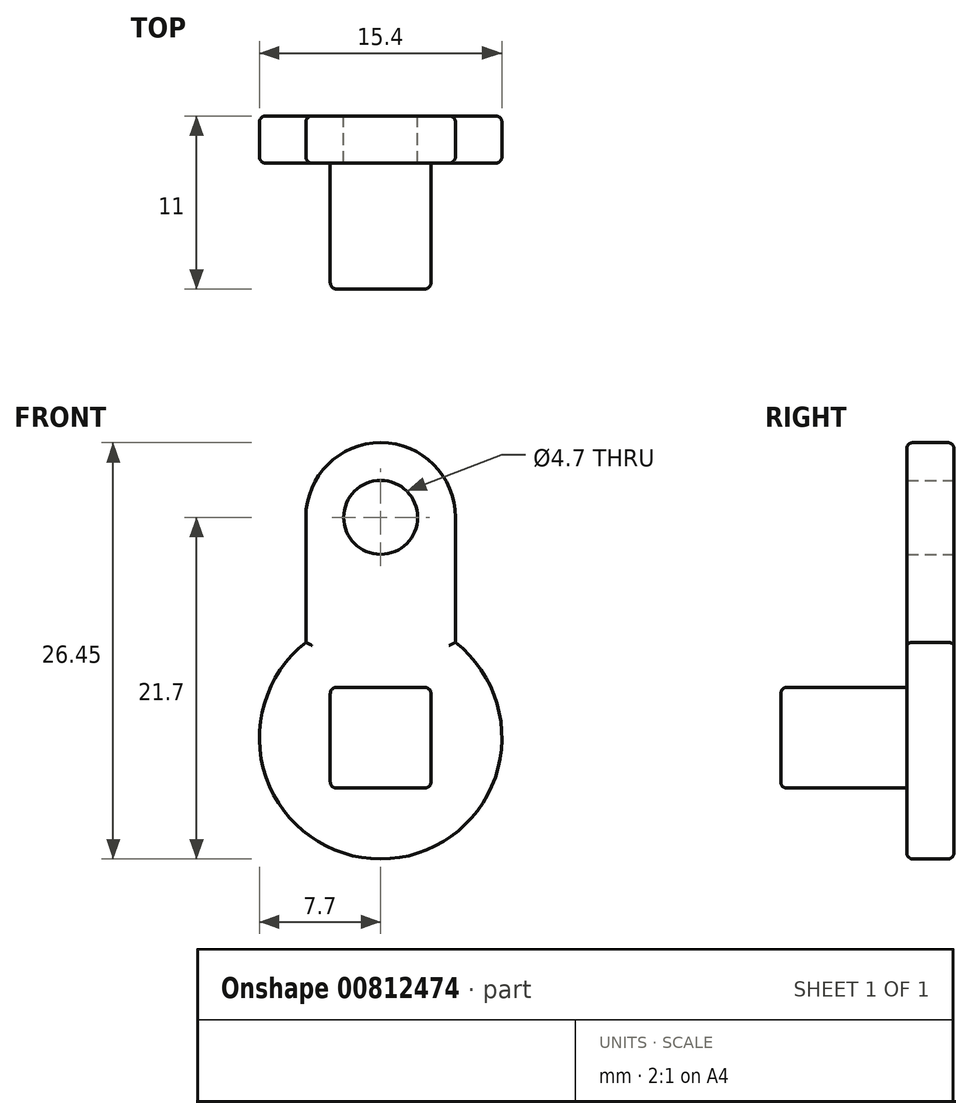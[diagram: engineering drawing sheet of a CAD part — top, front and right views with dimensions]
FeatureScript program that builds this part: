
annotation { "Feature Type Name" : "Feature", "Feature Type Description" : "" }
export const myFeature = defineFeature(function(context is Context, id is Id, definition is map)
    precondition{}
    {
        {
            var Q0;
            Q0=qCreatedBy(makeId("Front.planeOp"),FACE);
            var sketch = newSketch(context, id + "F0", { "sketchPlane" : qUnion([Q0])});
            skCircle(sketch, "E0", {"center": v(0, 0) * mm, "radius": 7.7 * mm});
            skCircle(sketch, "E1", {"center": v(0, 14) * mm, "radius": 4.75 * mm});
            skLineSegment(sketch, "E2", {"start": v(-4.75, 14.01) * mm, "end": v(-4.75, 6.06) * mm});
            skLineSegment(sketch, "E3", {"start": v(4.75, 14) * mm, "end": v(4.75, 6.06) * mm});
            skCircle(sketch, "E4", {"center": v(0, 14) * mm, "radius": 2.35 * mm});
            skSolve(sketch);
        }
        {
            var Q0;
            Q0 = qSketchRegion(id + "F0", true);
            extrude(context, id + "F1", {"entities" : qUnion([Q0]), "depth" : 3 * mm, "offsetDistance" : 25 * mm});
        }
        {
            var Q0;
            Q0=makeQuery(id+"F1.opExtrude","CAP_FACE",FACE,{"disambiguationData":[OSD([sQuery(id+"F0.wireOp",EDGE,"E0"),sQuery(id+"F0.wireOp",EDGE,"E1"),sQuery(id+"F0.wireOp",EDGE,"E2"),sQuery(id+"F0.wireOp",EDGE,"E3"),sQuery(id+"F0.wireOp",EDGE,"E4")])],"isStart":false});
            var sketch = newSketch(context, id + "F2", { "sketchPlane" : qUnion([Q0])});
            skLineSegment(sketch, "E5.bottom", {"start": v(-3.2, 3.2) * mm, "end": v(3.2, 3.2) * mm});
            skLineSegment(sketch, "E5.top", {"start": v(-3.2, -3.2) * mm, "end": v(3.2, -3.2) * mm});
            skLineSegment(sketch, "E5.left", {"start": v(-3.2, 3.2) * mm, "end": v(-3.2, -3.2) * mm});
            skLineSegment(sketch, "E5.right", {"start": v(3.2, 3.2) * mm, "end": v(3.2, -3.2) * mm});
            skSolve(sketch);
        }
        {
            var Q0;
            Q0=makeQuery(id+"F2.imprint","IMPRINT",FACE,{"disambiguationData":[TD([[makeQuery(id+"F2.imprint","IMPRINT",EDGE,{"derivedFrom":sQuery(id+"F2.wireOp",EDGE,"E5.bottom")}),-1.0]])]});
            extrude(context, id + "F3", {"entities" : qUnion([Q0]), "operationType" : NewBodyOperationType.ADD, "depth" : 8 * mm, "offsetDistance" : 25 * mm});
        }
        {
            var Q0;
            Q0=makeQuery(id+"F3.opExtrude","CAP_EDGE",EDGE,{"disambiguationData":[OSD([sQuery(id+"F2.wireOp",EDGE,"E5.left")])],"isStart":false});
            var Q1;
            Q1=makeQuery(id+"F3.opExtrude","SWEPT_EDGE",EDGE,{"disambiguationData":[OSD([sQuery(id+"F2.wireOp",EDGE,"E5.bottom"),sQuery(id+"F2.wireOp",EDGE,"E5.left")])]});
            var Q2;
            Q2=makeQuery(id+"F3.opExtrude","CAP_EDGE",EDGE,{"disambiguationData":[OSD([sQuery(id+"F2.wireOp",EDGE,"E5.bottom")])],"isStart":false});
            var Q3;
            Q3=makeQuery(id+"F3.opExtrude","CAP_EDGE",EDGE,{"disambiguationData":[OSD([sQuery(id+"F2.wireOp",EDGE,"E5.top")])],"isStart":false});
            var Q4;
            Q4=makeQuery(id+"F3.opExtrude","CAP_EDGE",EDGE,{"disambiguationData":[OSD([sQuery(id+"F2.wireOp",EDGE,"E5.right")])],"isStart":false});
            var Q5;
            Q5=makeQuery(id+"F3.opExtrude","SWEPT_EDGE",EDGE,{"disambiguationData":[OSD([sQuery(id+"F2.wireOp",EDGE,"E5.top"),sQuery(id+"F2.wireOp",EDGE,"E5.right")])]});
            var Q6;
            Q6=makeQuery(id+"F3.opExtrude","SWEPT_EDGE",EDGE,{"disambiguationData":[OSD([sQuery(id+"F2.wireOp",EDGE,"E5.bottom"),sQuery(id+"F2.wireOp",EDGE,"E5.right")])]});
            var Q7;
            Q7=makeQuery(id+"F1.opExtrude","CAP_EDGE",EDGE,{"disambiguationData":[OSD([sQuery(id+"F0.wireOp",EDGE,"E0")])],"isStart":false});
            var Q8;
            Q8=makeQuery(id+"F1.opExtrude","CAP_EDGE",EDGE,{"disambiguationData":[OSD([sQuery(id+"F0.wireOp",EDGE,"E3")])],"isStart":false});
            var Q9;
            Q9=makeQuery(id+"F1.opExtrude","CAP_EDGE",EDGE,{"disambiguationData":[OSD([sQuery(id+"F0.wireOp",EDGE,"E1")])],"isStart":false});
            var Q10;
            Q10=makeQuery(id+"F1.opExtrude","CAP_EDGE",EDGE,{"disambiguationData":[OSD([sQuery(id+"F0.wireOp",EDGE,"E2")])],"isStart":false});
            var Q11;
            Q11=makeQuery(id+"F1.opExtrude","CAP_EDGE",EDGE,{"disambiguationData":[OSD([sQuery(id+"F0.wireOp",EDGE,"E0")])],"isStart":true});
            var Q12;
            Q12=makeQuery(id+"F1.opExtrude","CAP_EDGE",EDGE,{"disambiguationData":[OSD([sQuery(id+"F0.wireOp",EDGE,"E3")])],"isStart":true});
            var Q13;
            Q13=makeQuery(id+"F1.opExtrude","CAP_EDGE",EDGE,{"disambiguationData":[OSD([sQuery(id+"F0.wireOp",EDGE,"E2")])],"isStart":true});
            var Q14;
            Q14=makeQuery(id+"F1.opExtrude","CAP_EDGE",EDGE,{"disambiguationData":[OSD([sQuery(id+"F0.wireOp",EDGE,"E1")])],"isStart":true});
            var Q15;
            Q15=makeQuery(id+"F3.opExtrude","SWEPT_EDGE",EDGE,{"disambiguationData":[OSD([sQuery(id+"F2.wireOp",EDGE,"E5.top"),sQuery(id+"F2.wireOp",EDGE,"E5.left")])]});
            fillet(context, id + "F4", {"entities" : qUnion([Q0, Q1, Q2, Q3, Q4, Q5, Q6, Q7, Q8, Q9, Q10, Q11, Q12, Q13, Q14, Q15]), "radius" : .4 * mm, "tangentPropagation" : true, "allowEdgeOverflow" : false});
        }
    });
